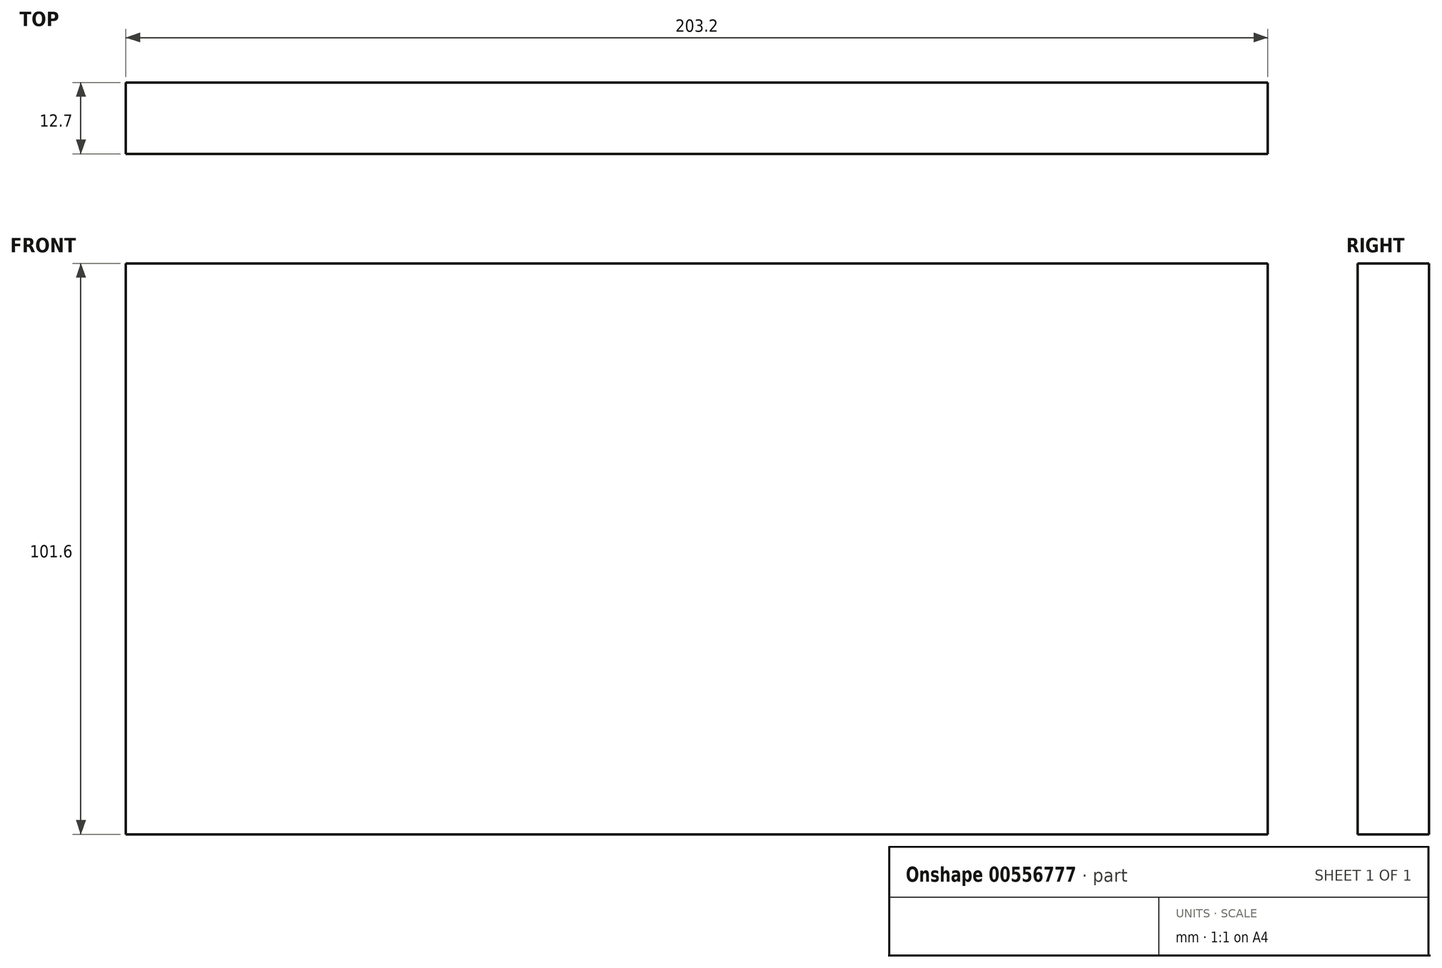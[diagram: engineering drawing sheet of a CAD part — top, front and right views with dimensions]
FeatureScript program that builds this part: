
annotation { "Feature Type Name" : "Feature", "Feature Type Description" : "" }
export const myFeature = defineFeature(function(context is Context, id is Id, definition is map)
    precondition{}
    {
        {
            var Q0;
            Q0=qCreatedBy(makeId("Front.planeOp"),FACE);
            var sketch = newSketch(context, id + "F0", { "sketchPlane" : qUnion([Q0])});
            skLineSegment(sketch, "E0.bottom", {"start": v(203.2, 101.6) * mm, "end": v(0, 101.6) * mm});
            skLineSegment(sketch, "E0.top", {"start": v(203.2, 0) * mm, "end": v(0, 0) * mm});
            skLineSegment(sketch, "E0.left", {"start": v(203.2, 101.6) * mm, "end": v(203.2, 0) * mm});
            skLineSegment(sketch, "E0.right", {"start": v(0, 101.6) * mm, "end": v(0, 0) * mm});
            skSolve(sketch);
        }
        {
            var Q0;
            Q0 = qSketchRegion(id + "F0", true);
            extrude(context, id + "F1", {"entities" : qUnion([Q0]), "oppositeDirection" : true, "depth" : 12.7 * mm, "offsetDistance" : 25.4 * mm});
        }
    });
